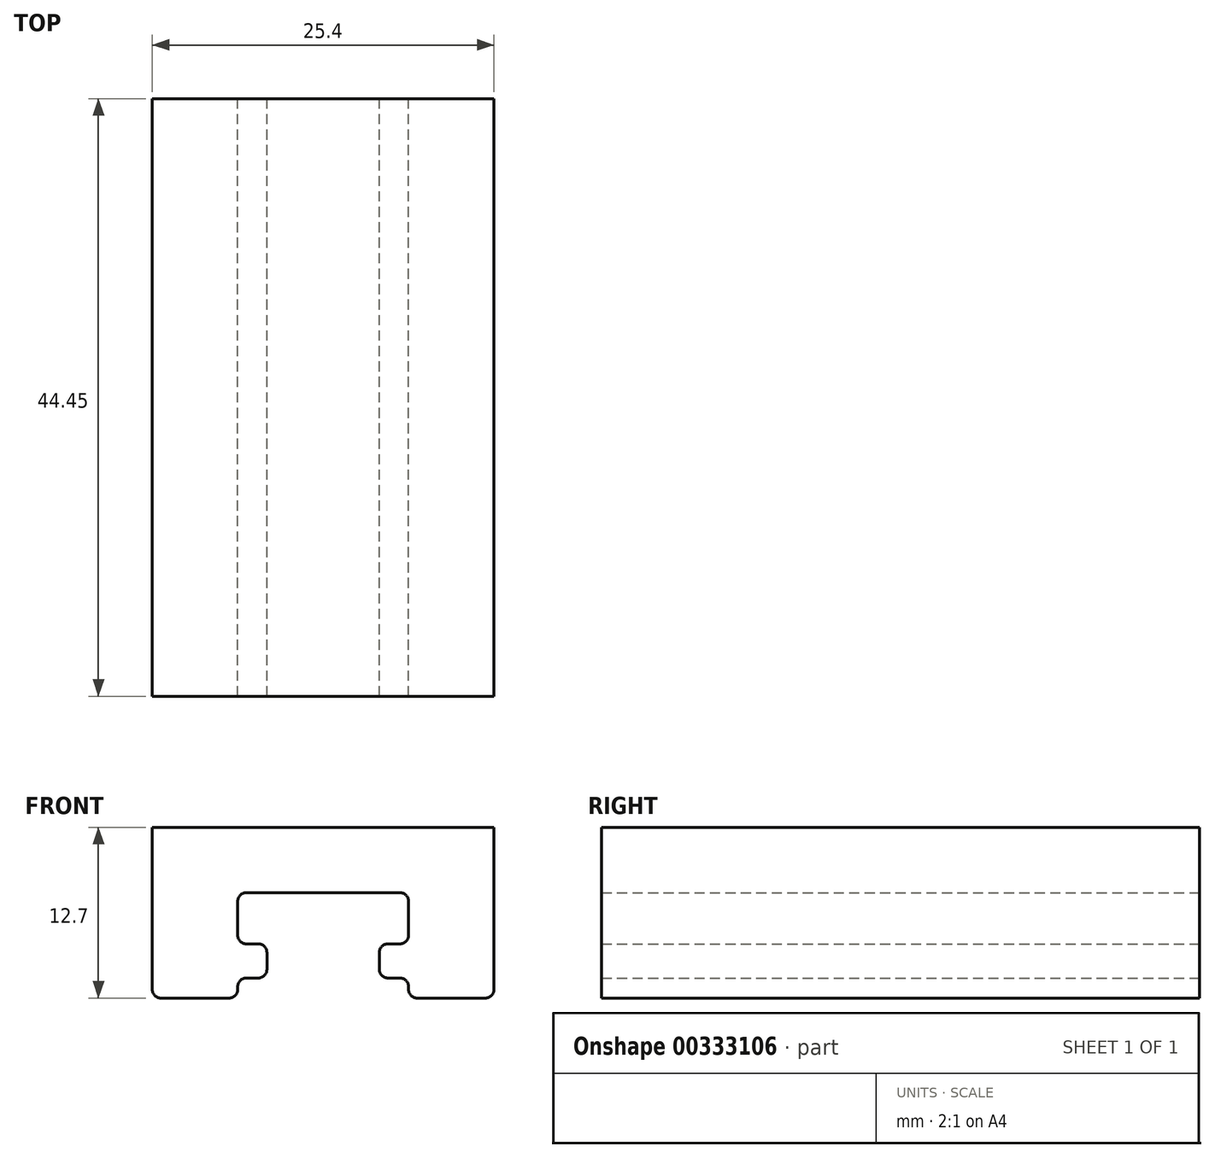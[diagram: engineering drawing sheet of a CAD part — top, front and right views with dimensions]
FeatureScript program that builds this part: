
annotation { "Feature Type Name" : "Feature", "Feature Type Description" : "" }
export const myFeature = defineFeature(function(context is Context, id is Id, definition is map)
    precondition{}
    {
        {
            var Q0;
            Q0=qCreatedBy(makeId("Front.planeOp"),FACE);
            var sketch = newSketch(context, id + "F0", { "sketchPlane" : qUnion([Q0])});
            skLineSegment(sketch, "E0", {"start": v(5.43, -6.4) * mm, "end": v(5.43, -4.9) * mm});
            skLineSegment(sketch, "E1", {"start": v(-7.27, -6.4) * mm, "end": v(-7.27, -4.9) * mm});
            skLineSegment(sketch, "E2", {"start": v(5.43, -4.9) * mm, "end": v(3.26, -4.9) * mm});
            skLineSegment(sketch, "E3", {"start": v(3.26, -4.9) * mm, "end": v(3.26, -2.36) * mm});
            skLineSegment(sketch, "E4", {"start": v(3.26, -2.36) * mm, "end": v(5.43, -2.36) * mm});
            skLineSegment(sketch, "E5", {"start": v(5.43, -2.36) * mm, "end": v(5.43, 1.45) * mm});
            skLineSegment(sketch, "E6", {"start": v(5.43, 1.45) * mm, "end": v(-7.27, 1.45) * mm});
            skLineSegment(sketch, "E7", {"start": v(-7.27, 1.45) * mm, "end": v(-7.27, -2.36) * mm});
            skLineSegment(sketch, "E8", {"start": v(-7.27, -2.36) * mm, "end": v(-5.1, -2.36) * mm});
            skLineSegment(sketch, "E9", {"start": v(-5.1, -2.36) * mm, "end": v(-5.1, -4.9) * mm});
            skLineSegment(sketch, "E10", {"start": v(-5.1, -4.9) * mm, "end": v(-7.27, -4.9) * mm});
            skLineSegment(sketch, "E11", {"start": v(5.43, -6.4) * mm, "end": v(11.78, -6.4) * mm});
            skLineSegment(sketch, "E12", {"start": v(11.78, -6.4) * mm, "end": v(11.78, 6.3) * mm});
            skLineSegment(sketch, "E13", {"start": v(11.78, 6.3) * mm, "end": v(-13.62, 6.3) * mm});
            skLineSegment(sketch, "E14", {"start": v(-13.62, 6.3) * mm, "end": v(-13.62, -6.4) * mm});
            skLineSegment(sketch, "E15", {"start": v(-13.62, -6.4) * mm, "end": v(-7.27, -6.4) * mm});
            skSolve(sketch);
        }
        {
            var Q0;
            Q0=qSketchRegion(id+"F0",true);
            extrude(context, id + "F1", {"entities" : qUnion([Q0]), "depth" : 44.45 * mm});
        }
        {
            var Q0;
            Q0=makeQuery(id+"F1.opExtrude","SWEPT_EDGE",EDGE,{"disambiguationData":[OSD([sQuery(id+"F0.wireOp",EDGE,"E6"),sQuery(id+"F0.wireOp",EDGE,"E7")])]});
            var Q1;
            Q1=makeQuery(id+"F1.opExtrude","SWEPT_EDGE",EDGE,{"disambiguationData":[OSD([sQuery(id+"F0.wireOp",EDGE,"E7"),sQuery(id+"F0.wireOp",EDGE,"E8")])]});
            var Q2;
            Q2=makeQuery(id+"F1.opExtrude","SWEPT_EDGE",EDGE,{"disambiguationData":[OSD([sQuery(id+"F0.wireOp",EDGE,"E8"),sQuery(id+"F0.wireOp",EDGE,"E9")])]});
            var Q3;
            Q3=makeQuery(id+"F1.opExtrude","SWEPT_EDGE",EDGE,{"disambiguationData":[OSD([sQuery(id+"F0.wireOp",EDGE,"E9"),sQuery(id+"F0.wireOp",EDGE,"E10")])]});
            var Q4;
            Q4=makeQuery(id+"F1.opExtrude","SWEPT_EDGE",EDGE,{"disambiguationData":[OSD([sQuery(id+"F0.wireOp",EDGE,"E1"),sQuery(id+"F0.wireOp",EDGE,"E10")])]});
            var Q5;
            Q5=makeQuery(id+"F1.opExtrude","SWEPT_EDGE",EDGE,{"disambiguationData":[OSD([sQuery(id+"F0.wireOp",EDGE,"E5"),sQuery(id+"F0.wireOp",EDGE,"E6")])]});
            var Q6;
            Q6=makeQuery(id+"F1.opExtrude","SWEPT_EDGE",EDGE,{"disambiguationData":[OSD([sQuery(id+"F0.wireOp",EDGE,"E4"),sQuery(id+"F0.wireOp",EDGE,"E5")])]});
            var Q7;
            Q7=makeQuery(id+"F1.opExtrude","SWEPT_EDGE",EDGE,{"disambiguationData":[OSD([sQuery(id+"F0.wireOp",EDGE,"E3"),sQuery(id+"F0.wireOp",EDGE,"E4")])]});
            var Q8;
            Q8=makeQuery(id+"F1.opExtrude","SWEPT_EDGE",EDGE,{"disambiguationData":[OSD([sQuery(id+"F0.wireOp",EDGE,"E2"),sQuery(id+"F0.wireOp",EDGE,"E3")])]});
            var Q9;
            Q9=makeQuery(id+"F1.opExtrude","SWEPT_EDGE",EDGE,{"disambiguationData":[OSD([sQuery(id+"F0.wireOp",EDGE,"E0"),sQuery(id+"F0.wireOp",EDGE,"E2")])]});
            var Q10;
            Q10=makeQuery(id+"F1.opExtrude","SWEPT_EDGE",EDGE,{"disambiguationData":[OSD([sQuery(id+"F0.wireOp",EDGE,"E1"),sQuery(id+"F0.wireOp",EDGE,"E15")])]});
            var Q11;
            Q11=makeQuery(id+"F1.opExtrude","SWEPT_EDGE",EDGE,{"disambiguationData":[OSD([sQuery(id+"F0.wireOp",EDGE,"E0"),sQuery(id+"F0.wireOp",EDGE,"E11")])]});
            var Q12;
            Q12=makeQuery(id+"F1.opExtrude","SWEPT_EDGE",EDGE,{"disambiguationData":[OSD([sQuery(id+"F0.wireOp",EDGE,"E11"),sQuery(id+"F0.wireOp",EDGE,"E12")])]});
            var Q13;
            Q13=makeQuery(id+"F1.opExtrude","SWEPT_EDGE",EDGE,{"disambiguationData":[OSD([sQuery(id+"F0.wireOp",EDGE,"E14"),sQuery(id+"F0.wireOp",EDGE,"E15")])]});
            fillet(context, id + "F2", {"entities" : qUnion([Q0, Q1, Q2, Q3, Q4, Q5, Q6, Q7, Q8, Q9, Q10, Q11, Q12, Q13]), "radius" : 0.64 * mm, "tangentPropagation" : true, "allowEdgeOverflow" : false});
        }
    });
